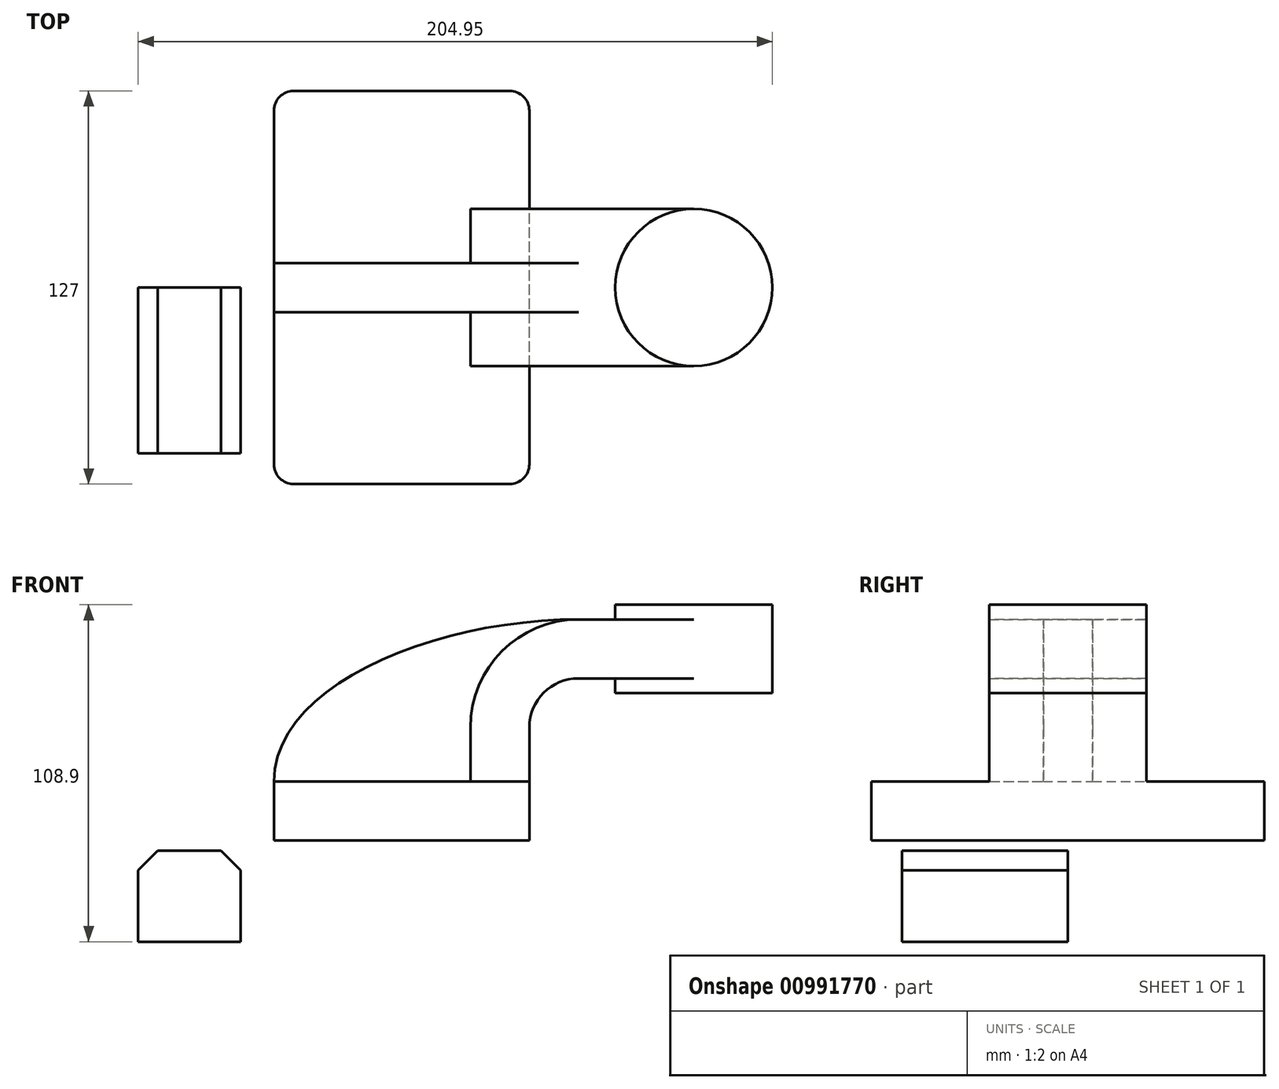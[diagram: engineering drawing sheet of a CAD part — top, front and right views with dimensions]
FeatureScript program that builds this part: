
annotation { "Feature Type Name" : "Feature", "Feature Type Description" : "" }
export const myFeature = defineFeature(function(context is Context, id is Id, definition is map)
    precondition{}
    {
        {
            var Q0;
            Q0=qCreatedBy(makeId("Front.planeOp"),FACE);
            var sketch = newSketch(context, id + "F0", { "sketchPlane" : qUnion([Q0])});
            skLineSegment(sketch, "E0.bottom", {"start": v(41.28, -9.52) * mm, "end": v(-41.28, -9.53) * mm});
            skLineSegment(sketch, "E0.top", {"start": v(41.28, 9.53) * mm, "end": v(-41.28, 9.52) * mm});
            skLineSegment(sketch, "E0.left", {"start": v(41.28, -9.52) * mm, "end": v(41.28, 9.53) * mm});
            skLineSegment(sketch, "E0.right", {"start": v(-41.28, -9.53) * mm, "end": v(-41.28, 9.52) * mm});
            skPoint(sketch, "E0.middle", {"position": v(0, 0) * mm});
            skLineSegment(sketch, "E1.bottom", {"start": v(119.83, 38.1) * mm, "end": v(69.03, 38.1) * mm});
            skLineSegment(sketch, "E1.top", {"start": v(119.83, 66.68) * mm, "end": v(69.03, 66.68) * mm});
            skLineSegment(sketch, "E1.left", {"start": v(119.83, 38.1) * mm, "end": v(119.83, 66.68) * mm});
            skLineSegment(sketch, "E1.right", {"start": v(69.03, 38.1) * mm, "end": v(69.03, 66.68) * mm});
            skPoint(sketch, "E1.middle", {"position": v(94.43, 52.39) * mm});
            skLineSegment(sketch, "E2", {"start": v(41.28, 27) * mm, "end": v(41.28, 9.53) * mm});
            skArc(sketch, "E3", {"start": v(41.27, 27) * mm, "mid": v(45.92, 38.23) * mm, "end": v(57.15, 42.88) * mm});
            skLineSegment(sketch, "E4", {"start": v(57.15, 42.88) * mm, "end": v(94.43, 42.88) * mm});
            skPoint(sketch, "E4.endSnap0", {"position": v(94.43, 38.1) * mm});
            skLineSegment(sketch, "E5.0", {"start": v(22.23, 27) * mm, "end": v(22.23, 9.53) * mm});
            skArc(sketch, "E5.1", {"start": v(22.23, 27) * mm, "mid": v(32.45, 51.7) * mm, "end": v(57.15, 61.93) * mm});
            skLineSegment(sketch, "E5.2", {"start": v(57.15, 61.93) * mm, "end": v(94.43, 61.93) * mm});
            skLineSegment(sketch, "E6", {"start": v(94.43, 61.93) * mm, "end": v(94.43, 42.88) * mm});
            skFitSpline(sketch, "E7", {"points": [v(-41.28, 9.52) * mm, v(57.15, 61.93) * mm], "startDerivative": vector(1.08, 96.3) * mm, "endDerivative": vector(135.28, -0.1) * mm});
            skLineSegment(sketch, "E8", {"start": v(94.43, 42.88) * mm, "end": v(94.43, 38.1) * mm});
            skLineSegment(sketch, "E9", {"start": v(94.43, 61.93) * mm, "end": v(94.43, 66.68) * mm});
            skLineSegment(sketch, "E10", {"start": v(94.43, 38.1) * mm, "end": v(94.43, 42.88) * mm});
            skSolve(sketch);
        }
        {
            var Q0;
            Q0=makeQuery(id+"F0.imprint","IMPRINT",FACE,{"disambiguationData":[TD([[makeQuery(id+"F0.imprint","IMPRINT",EDGE,{"derivedFrom":sQuery(id+"F0.wireOp",EDGE,"E0.bottom")}),-1.0]])]});
            extrude(context, id + "F1", {"entities" : qUnion([Q0]), "endBound" : BoundingType.SYMMETRIC, "depth" : 127 * mm, "offsetDistance" : 25.4 * mm});
        }
        {
            var Q0;
            {var subQ1=sQuery(id+"F0.wireOp",EDGE,"E2");Q0=makeQuery(id+"F0.imprint","IMPRINT",FACE,{"disambiguationData":[TD([[makeQuery(id+"F0.imprint","IMPRINT",EDGE,{"derivedFrom":subQ1}),-1.0]])]});}
            var Q1;
            {var subQ5=sQuery(id+"F0.wireOp",EDGE,"E6");Q1=makeQuery(id+"F0.imprint","IMPRINT",FACE,{"disambiguationData":[TD([[makeQuery(id+"F0.imprint","IMPRINT",EDGE,{"derivedFrom":subQ5}),-1.0]])]});}
            extrude(context, id + "F2", {"entities" : qUnion([Q0, Q1]), "operationType" : NewBodyOperationType.ADD, "endBound" : BoundingType.SYMMETRIC, "depth" : 50.8 * mm, "offsetDistance" : 25.4 * mm});
        }
        {
            var Q0;
            {var subQ2=sQuery(id+"F0.wireOp",EDGE,"E5.0");Q0=makeQuery(id+"F0.imprint","IMPRINT",FACE,{"disambiguationData":[TD([[makeQuery(id+"F0.imprint","IMPRINT",EDGE,{"derivedFrom":subQ2}),-1.0]])]});}
            extrude(context, id + "F3", {"entities" : qUnion([Q0]), "operationType" : NewBodyOperationType.ADD, "endBound" : BoundingType.SYMMETRIC, "depth" : 15.88 * mm, "offsetDistance" : 25.4 * mm});
        }
        {
            var Q0;
            {var subQ0=sQuery(id+"F0.wireOp",EDGE,"E1.left");Q0=makeQuery(id+"F0.imprint","IMPRINT",FACE,{"disambiguationData":[TD([[makeQuery(id+"F0.imprint","IMPRINT",EDGE,{"derivedFrom":subQ0}),1.0]])]});}
            var Q1;
            Q1=sQuery(id+"F0.wireOp",EDGE,"E6");
            revolve(context, id + "F4", {"operationType" : NewBodyOperationType.ADD, "surfaceOperationType" : NewSurfaceOperationType.NEW, "entities" : qUnion([Q0]), "axis" : qUnion([Q1]), "revolveType" : RevolveType.FULL});
        }
        {
            var Q0;
            Q0=makeQuery(id+"F1.opExtrude","CAP_EDGE",EDGE,{"disambiguationData":[OSD([sQuery(id+"F0.wireOp",EDGE,"E0.right")])],"isStart":false});
            var Q1;
            Q1=makeQuery(id+"F1.opExtrude","CAP_EDGE",EDGE,{"disambiguationData":[OSD([sQuery(id+"F0.wireOp",EDGE,"E0.left")])],"isStart":false});
            var Q2;
            Q2=makeQuery(id+"F1.opExtrude","CAP_EDGE",EDGE,{"disambiguationData":[OSD([sQuery(id+"F0.wireOp",EDGE,"E0.left")])],"isStart":true});
            var Q3;
            Q3=makeQuery(id+"F1.opExtrude","CAP_EDGE",EDGE,{"disambiguationData":[OSD([sQuery(id+"F0.wireOp",EDGE,"E0.right")])],"isStart":true});
            fillet(context, id + "F5", {"entities" : qUnion([Q0, Q1, Q2, Q3]), "radius" : 6.35 * mm, "tangentPropagation" : true, "allowEdgeOverflow" : false});
        }
        {
            var Q0;
            Q0=qCreatedBy(makeId("Front.planeOp"),FACE);
            var sketch = newSketch(context, id + "F6", { "sketchPlane" : qUnion([Q0])});
            skLineSegment(sketch, "E11.bottom", {"start": v(-52.07, -42.22) * mm, "end": v(-85.12, -42.22) * mm});
            skLineSegment(sketch, "E11.top", {"start": v(-52.07, -12.85) * mm, "end": v(-85.12, -12.85) * mm});
            skLineSegment(sketch, "E11.left", {"start": v(-52.07, -42.22) * mm, "end": v(-52.07, -12.85) * mm});
            skLineSegment(sketch, "E11.right", {"start": v(-85.12, -42.22) * mm, "end": v(-85.12, -12.85) * mm});
            skPoint(sketch, "E11.middle", {"position": v(-68.6, -27.54) * mm});
            skSolve(sketch);
        }
        {
            var Q0;
            Q0 = qSketchRegion(id + "F6", true);
            extrude(context, id + "F7", {"entities" : qUnion([Q0]), "depth" : 53.6 * mm, "offsetDistance" : 25.4 * mm});
        }
        {
            var Q0;
            Q0=makeQuery(id+"F7.opExtrude","SWEPT_EDGE",EDGE,{"disambiguationData":[OSD([sQuery(id+"F6.wireOp",EDGE,"E11.top"),sQuery(id+"F6.wireOp",EDGE,"E11.right")])]});
            var Q1;
            Q1=makeQuery(id+"F7.opExtrude","SWEPT_EDGE",EDGE,{"disambiguationData":[OSD([sQuery(id+"F6.wireOp",EDGE,"E11.top"),sQuery(id+"F6.wireOp",EDGE,"E11.left")])]});
            chamfer(context, id + "F8", {"entities" : qUnion([Q0, Q1]), "width" : 6.35 * mm, "tangentPropagation" : true});
        }
    });
